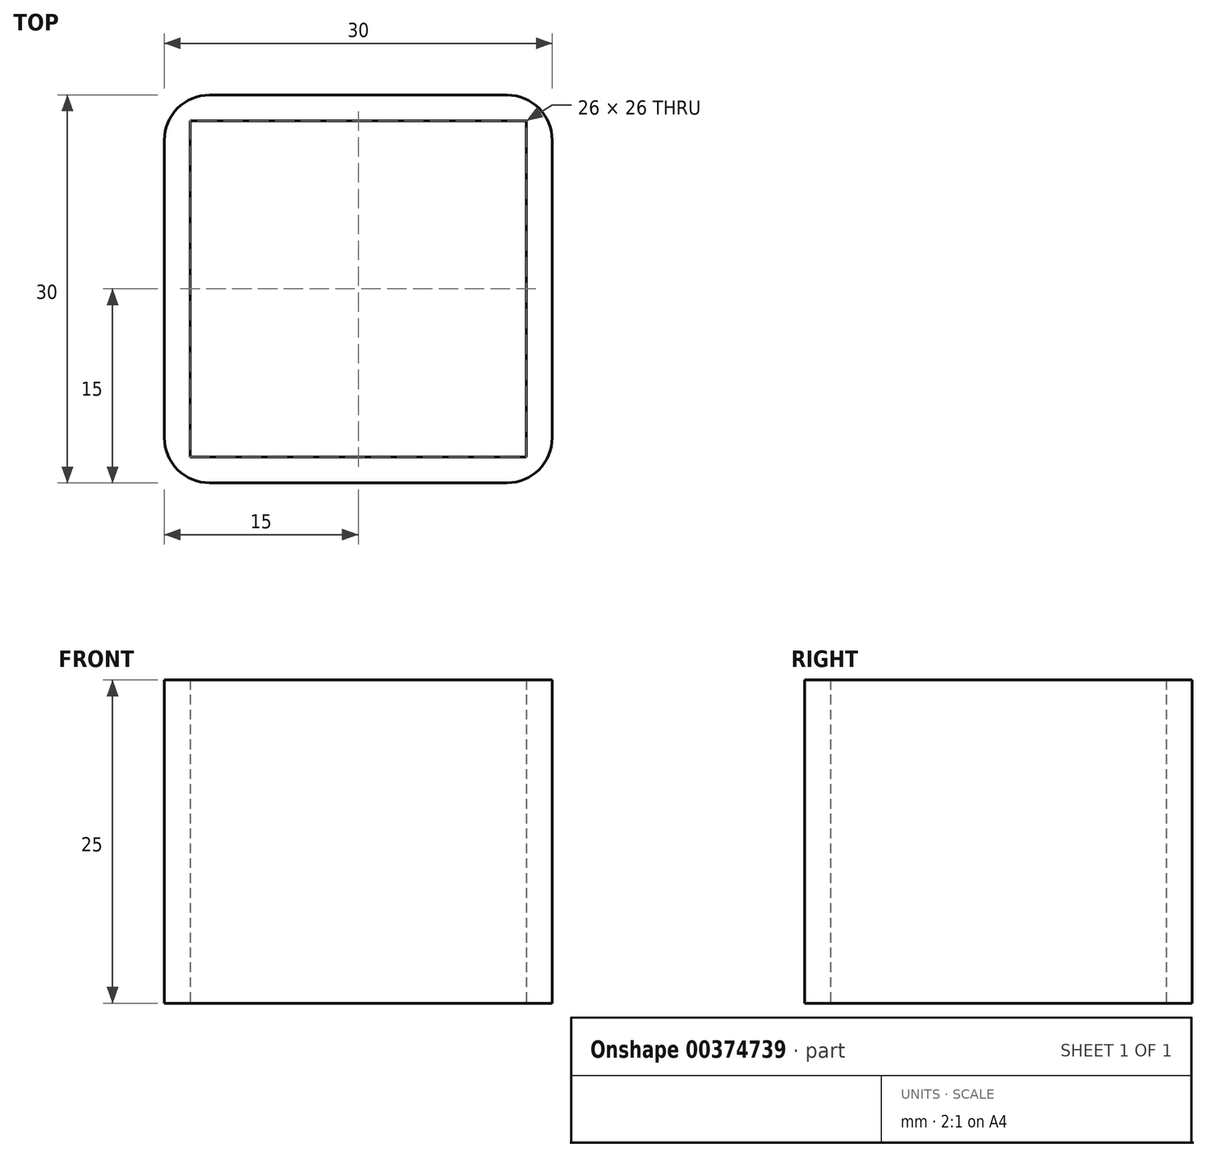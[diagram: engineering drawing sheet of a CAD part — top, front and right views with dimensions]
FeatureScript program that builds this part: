
annotation { "Feature Type Name" : "Feature", "Feature Type Description" : "" }
export const myFeature = defineFeature(function(context is Context, id is Id, definition is map)
    precondition{}
    {
        {
            var Q0;
            Q0=qCreatedBy(makeId("Top.planeOp"),FACE);
            var sketch = newSketch(context, id + "F0", { "sketchPlane" : qUnion([Q0])});
            skLineSegment(sketch, "E0.bottom", {"start": v(11.5, 15) * mm, "end": v(-11.5, 15) * mm});
            skLineSegment(sketch, "E0.top", {"start": v(11.5, -15) * mm, "end": v(-11.5, -15) * mm});
            skLineSegment(sketch, "E0.left", {"start": v(15, 11.5) * mm, "end": v(15, -11.5) * mm});
            skLineSegment(sketch, "E0.right", {"start": v(-15, 11.5) * mm, "end": v(-15, -11.5) * mm});
            skPoint(sketch, "E0.middle", {"position": v(0, 0) * mm});
            skLineSegment(sketch, "E1.bottom", {"start": v(13, 13) * mm, "end": v(-13, 13) * mm});
            skLineSegment(sketch, "E1.top", {"start": v(13, -13) * mm, "end": v(-13, -13) * mm});
            skLineSegment(sketch, "E1.left", {"start": v(13, 13) * mm, "end": v(13, -13) * mm});
            skLineSegment(sketch, "E1.right", {"start": v(-13, 13) * mm, "end": v(-13, -13) * mm});
            skPoint(sketch, "E2.visualSharp", {"position": v(-15, 15) * mm});
            skArc(sketch, "E2.filletArc", {"start": v(-11.5, 15) * mm, "mid": v(-13.97, 13.97) * mm, "end": v(-15, 11.5) * mm});
            skPoint(sketch, "E3.visualSharp", {"position": v(15, 15) * mm});
            skArc(sketch, "E3.filletArc", {"start": v(15, 11.5) * mm, "mid": v(13.97, 13.97) * mm, "end": v(11.5, 15) * mm});
            skPoint(sketch, "E4.visualSharp", {"position": v(15, -15) * mm});
            skArc(sketch, "E4.filletArc", {"start": v(11.5, -15) * mm, "mid": v(13.97, -13.97) * mm, "end": v(15, -11.5) * mm});
            skPoint(sketch, "E5.visualSharp", {"position": v(-15, -15) * mm});
            skArc(sketch, "E5.filletArc", {"start": v(-15, -11.5) * mm, "mid": v(-13.97, -13.97) * mm, "end": v(-11.5, -15) * mm});
            skSolve(sketch);
        }
        {
            var Q0;
            Q0=makeQuery(id+"F0.imprint","IMPRINT",FACE,{"disambiguationData":[TD([[makeQuery(id+"F0.imprint","IMPRINT",EDGE,{"derivedFrom":sQuery(id+"F0.wireOp",EDGE,"E0.bottom")}),1.0]])]});
            extrude(context, id + "F1", {"entities" : qUnion([Q0]), "depth" : 25 * mm});
        }
    });
